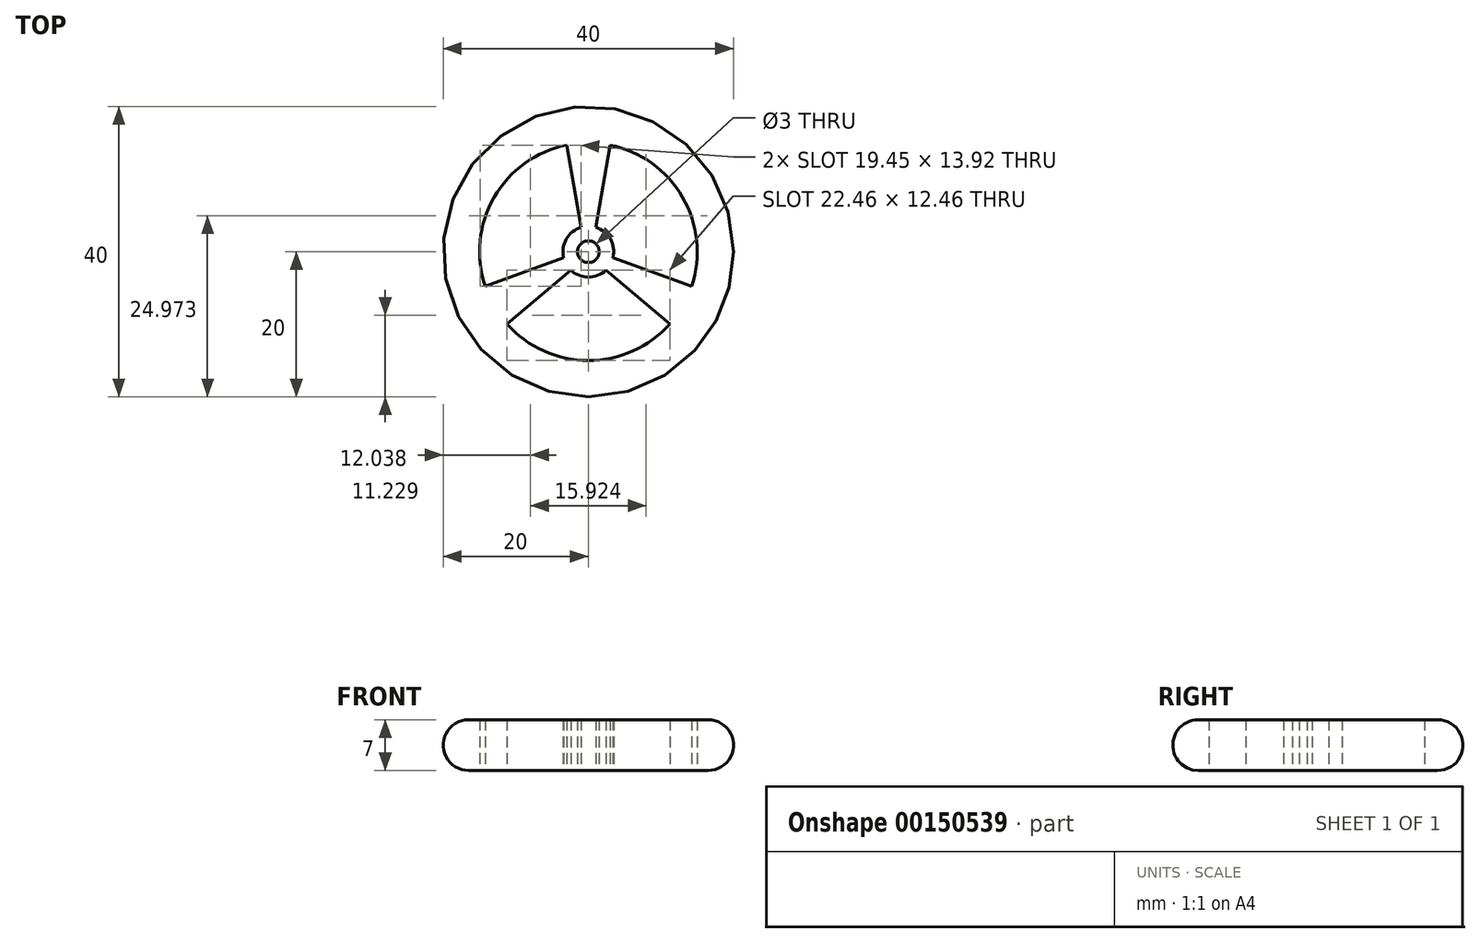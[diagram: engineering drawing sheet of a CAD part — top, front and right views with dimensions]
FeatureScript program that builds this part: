
annotation { "Feature Type Name" : "Feature", "Feature Type Description" : "" }
export const myFeature = defineFeature(function(context is Context, id is Id, definition is map)
    precondition{}
    {
        {
            var Q0;
            Q0=qCreatedBy(makeId("Top.planeOp"),FACE);
            var sketch = newSketch(context, id + "F0", { "sketchPlane" : qUnion([Q0])});
            skCircle(sketch, "E0", {"center": v(0, 0) * mm, "radius": 20 * mm});
            skArc(sketch, "E1", {"start": v(-3, 14.7) * mm, "mid": v(-13, 7.5) * mm, "end": v(-14.23, -4.75) * mm});
            skArc(sketch, "E2", {"start": v(-1, 3.35) * mm, "mid": v(-3.03, 1.75) * mm, "end": v(-3.4, -0.81) * mm});
            skCircle(sketch, "E3", {"center": v(0, 0) * mm, "radius": 1.5 * mm});
            skLineSegment(sketch, "E4", {"start": v(0, 0) * mm, "end": v(0, 20) * mm, "construction": true});
            skLineSegment(sketch, "E5", {"start": v(-1, 3.35) * mm, "end": v(-3, 14.7) * mm});
            skLineSegment(sketch, "E6.MirrorCS", {"start": v(1, 3.35) * mm, "end": v(3, 14.7) * mm});
            skLineSegment(sketch, "E7.1.0", {"start": v(-2.4, -2.54) * mm, "end": v(-11.23, -9.95) * mm});
            skLineSegment(sketch, "E7.1.1", {"start": v(-3.4, -0.81) * mm, "end": v(-14.23, -4.75) * mm});
            skLineSegment(sketch, "E7.2.0", {"start": v(3.4, -0.81) * mm, "end": v(14.23, -4.75) * mm});
            skLineSegment(sketch, "E7.2.1", {"start": v(2.4, -2.54) * mm, "end": v(11.23, -9.95) * mm});
            skArc(sketch, "E8.trimOffspring", {"start": v(-2.4, -2.54) * mm, "mid": v(0, -3.5) * mm, "end": v(2.4, -2.54) * mm});
            skArc(sketch, "E9.trimOffspring", {"start": v(3.4, -0.81) * mm, "mid": v(3.03, 1.75) * mm, "end": v(1, 3.35) * mm});
            skArc(sketch, "E10.trimOffspring", {"start": v(14.23, -4.75) * mm, "mid": v(13, 7.5) * mm, "end": v(3, 14.7) * mm});
            skArc(sketch, "E11.trimOffspring", {"start": v(-11.23, -9.95) * mm, "mid": v(0, -15) * mm, "end": v(11.23, -9.95) * mm});
            skSolve(sketch);
        }
        {
            var Q0;
            Q0=makeQuery(id+"F0.imprint","IMPRINT",FACE,{"disambiguationData":[TD([[makeQuery(id+"F0.imprint","IMPRINT",EDGE,{"derivedFrom":sQuery(id+"F0.wireOp",EDGE,"E0")}),1.0]])]});
            extrude(context, id + "F1", {"entities" : qUnion([Q0]), "depth" : 7 * mm});
        }
        {
            var Q0;
            Q0=makeQuery(id+"F1.opExtrude","CAP_EDGE",EDGE,{"disambiguationData":[OSD([sQuery(id+"F0.wireOp",EDGE,"E0")])],"isStart":false});
            var Q1;
            Q1=makeQuery(id+"F1.opExtrude","CAP_EDGE",EDGE,{"disambiguationData":[OSD([sQuery(id+"F0.wireOp",EDGE,"E0")])],"isStart":true});
            fillet(context, id + "F2", {"entities" : qUnion([Q0, Q1]), "radius" : 3.5 * mm, "tangentPropagation" : true, "allowEdgeOverflow" : false});
        }
    });
